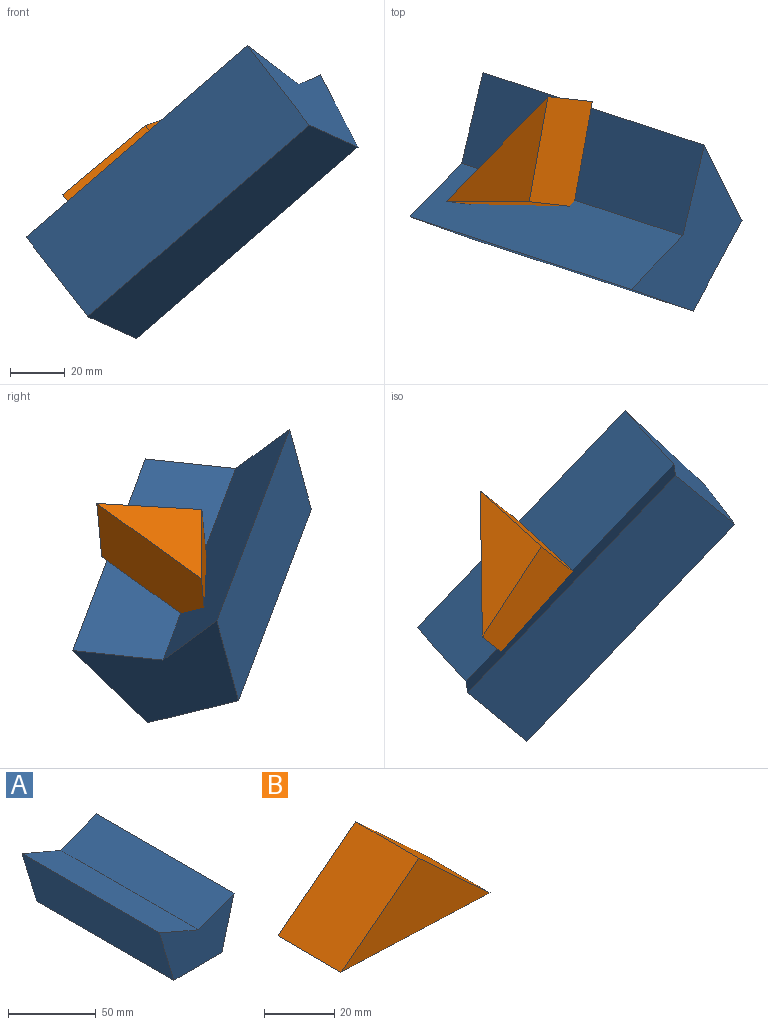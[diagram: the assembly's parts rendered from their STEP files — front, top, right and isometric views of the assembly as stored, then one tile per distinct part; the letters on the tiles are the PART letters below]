
ASSEMBLY  parts=2 mates=1
PART A: 7 faces, bbox 60.2x110.5x38.9 mm
  f0: plane 110.49x38.57mm, normal (0,0,-1), area 4261.2mm2, adj f1,f4,f5,f6
  f1: plane 110.49x36.55mm, normal (0.97,0,-0.26), area 4180.8mm2, adj f0,f2,f5,f6
  f2: plane 110.49x28.78mm, normal (-0.36,0,0.93), area 3413.2mm2, adj f1,f3,f5,f6
  f3: plane 110.49x31.37mm, normal (0.4,0,0.92), area 3774.7mm2, adj f2,f4,f5,f6
  f4: plane 110.49x38.85mm, normal (-0.96,0,-0.29), area 4486.6mm2, adj f0,f3,f5,f6
  f5: plane 60.15x38.85mm, normal (0,-1,0), area 1489.1mm2, adj f0,f1,f2,f3,f4
  f6: plane 60.15x38.85mm, normal (0,1,0), area 1489.1mm2, adj f0,f1,f2,f3,f4
PART B: 5 faces, bbox 60.2x25.4x26.6 mm
  f0: plane 28.78x26.55mm, normal (0.68,0,0.74), area 994.6mm2, adj f1,f2,f3,f4
  f1: plane 60.15x25.4mm, normal (-0.04,0,-1), area 1529mm2, adj f0,f2,f3,f4
  f2: plane 31.37x25.4mm, normal (-0.61,0,0.79), area 1007.1mm2, adj f0,f1,f3,f4
  f3: plane 60.15x26.55mm, normal (0,1,0), area 765.4mm2, adj f0,f1,f2
  f4: plane 60.15x26.55mm, normal (0,-1,0), area 765.4mm2, adj f0,f1,f2
PLACE A rot(axis=(0.11,-0.4,-0.91),118.7deg) t=(105.09,-65.22,89.88)mm
PLACE B rot(axis=(0.78,-0.02,0.62),86deg) t=(48.76,-24.69,39.08)mm
MATE revolute B.f4 <-> A.f3  axis (0.64,-0.07,-0.77) through (68.48,-35.35,56.54)mm
